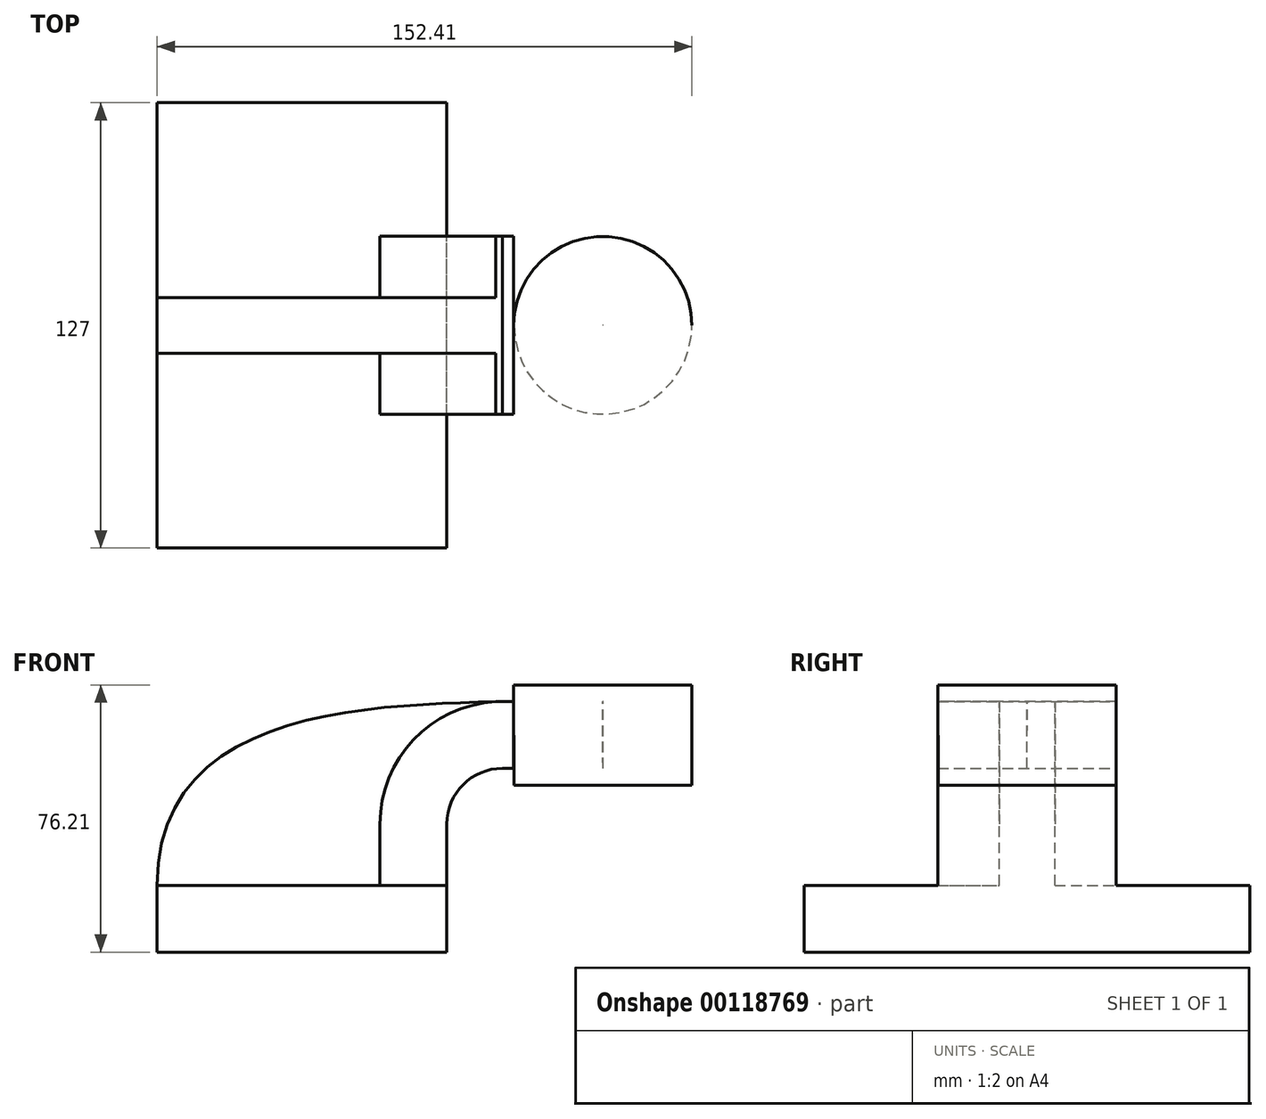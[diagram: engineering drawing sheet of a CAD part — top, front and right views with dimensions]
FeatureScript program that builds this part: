
annotation { "Feature Type Name" : "Feature", "Feature Type Description" : "" }
export const myFeature = defineFeature(function(context is Context, id is Id, definition is map)
    precondition{}
    {
        {
            var Q0;
            Q0=qCreatedBy(makeId("Front.planeOp"),FACE);
            var sketch = newSketch(context, id + "F0", { "sketchPlane" : qUnion([Q0])});
            skLineSegment(sketch, "E0.bottom", {"start": v(-41.28, 9.53) * mm, "end": v(41.28, 9.53) * mm});
            skLineSegment(sketch, "E0.top", {"start": v(-41.28, -9.53) * mm, "end": v(41.28, -9.53) * mm});
            skLineSegment(sketch, "E0.left", {"start": v(-41.28, 9.52) * mm, "end": v(-41.28, -9.53) * mm});
            skLineSegment(sketch, "E0.right", {"start": v(41.27, 9.53) * mm, "end": v(41.27, -9.52) * mm});
            skPoint(sketch, "E0.middle", {"position": v(0, 0) * mm});
            skLineSegment(sketch, "E1.bottom", {"start": v(111.12, 66.67) * mm, "end": v(60.32, 66.67) * mm});
            skLineSegment(sketch, "E1.top", {"start": v(111.12, 38.1) * mm, "end": v(85.79, 38.1) * mm});
            skLineSegment(sketch, "E1.left", {"start": v(111.12, 66.68) * mm, "end": v(111.12, 38.1) * mm});
            skLineSegment(sketch, "E1.right", {"start": v(60.32, 66.68) * mm, "end": v(60.32, 38.1) * mm});
            skPoint(sketch, "E1.middle", {"position": v(85.72, 52.39) * mm});
            skLineSegment(sketch, "E2", {"start": v(41.27, 9.53) * mm, "end": v(41.27, 27) * mm});
            skArc(sketch, "E3", {"start": v(41.27, 27) * mm, "mid": v(45.92, 38.23) * mm, "end": v(57.15, 42.88) * mm});
            skLineSegment(sketch, "E4.0", {"start": v(57.15, 61.93) * mm, "end": v(85.79, 61.93) * mm});
            skArc(sketch, "E4.1", {"start": v(22.22, 27) * mm, "mid": v(32.45, 51.7) * mm, "end": v(57.15, 61.93) * mm});
            skLineSegment(sketch, "E4.2", {"start": v(22.22, 9.53) * mm, "end": v(22.22, 27) * mm});
            skFitSpline(sketch, "E5", {"points": [v(-41.28, 9.52) * mm, v(57.15, 61.93) * mm], "startDerivative": vector(-0.32, 154.05) * mm, "endDerivative": vector(107.42, 3.15) * mm});
            skLineSegment(sketch, "E6", {"start": v(85.73, 66.67) * mm, "end": v(85.79, 38.1) * mm});
            skPoint(sketch, "E7.end.orphan", {"position": v(85.72, 42.88) * mm});
            skLineSegment(sketch, "E8", {"start": v(57.15, 42.88) * mm, "end": v(85.72, 42.88) * mm});
            skLineSegment(sketch, "E9", {"start": v(60.32, 38.1) * mm, "end": v(85.79, 38.1) * mm});
            skLineSegment(sketch, "E10.bottom", {"start": v(60.32, 42.88) * mm, "end": v(85.79, 42.88) * mm});
            skLineSegment(sketch, "E10.top", {"start": v(60.32, 61.93) * mm, "end": v(85.79, 61.93) * mm});
            skLineSegment(sketch, "E10.left", {"start": v(60.32, 42.88) * mm, "end": v(60.32, 61.93) * mm});
            skLineSegment(sketch, "E10.right", {"start": v(85.79, 42.88) * mm, "end": v(85.79, 61.93) * mm});
            skSolve(sketch);
        }
        {
            var Q0;
            Q0=makeQuery(id+"F0.imprint","IMPRINT",FACE,{"disambiguationData":[TD([[makeQuery(id+"F0.imprint","IMPRINT",EDGE,{"derivedFrom":sQuery(id+"F0.wireOp",EDGE,"E0.top")}),1.0]])]});
            extrude(context, id + "F1", {"entities" : qUnion([Q0]), "endBound" : BoundingType.SYMMETRIC, "depth" : 127 * mm});
        }
        {
            var Q0;
            {var subQ2=sQuery(id+"F0.wireOp",EDGE,"E2");Q0=makeQuery(id+"F0.imprint","IMPRINT",FACE,{"disambiguationData":[TD([[makeQuery(id+"F0.imprint","IMPRINT",EDGE,{"derivedFrom":subQ2}),1.0]])]});}
            var Q1;
            {var subQ0=sQuery(id+"F0.wireOp",EDGE,"E10.left");Q1=makeQuery(id+"F0.imprint","IMPRINT",FACE,{"disambiguationData":[TD([[makeQuery(id+"F0.imprint","IMPRINT",EDGE,{"derivedFrom":subQ0}),-1.0]])]});}
            extrude(context, id + "F2", {"entities" : qUnion([Q0, Q1]), "operationType" : NewBodyOperationType.ADD, "endBound" : BoundingType.SYMMETRIC, "depth" : 50.8 * mm});
        }
        {
            var Q0;
            {var subQ3=sQuery(id+"F0.wireOp",EDGE,"E4.2");Q0=makeQuery(id+"F0.imprint","IMPRINT",FACE,{"disambiguationData":[TD([[makeQuery(id+"F0.imprint","IMPRINT",EDGE,{"derivedFrom":subQ3}),1.0]])]});}
            extrude(context, id + "F3", {"entities" : qUnion([Q0]), "operationType" : NewBodyOperationType.ADD, "endBound" : BoundingType.SYMMETRIC, "depth" : 15.88 * mm});
        }
        {
            var Q0;
            {var subQ4=sQuery(id+"F0.wireOp",EDGE,"E1.left");Q0=makeQuery(id+"F0.imprint","IMPRINT",FACE,{"disambiguationData":[TD([[makeQuery(id+"F0.imprint","IMPRINT",EDGE,{"derivedFrom":subQ4}),-1.0]])]});}
            var Q1;
            Q1=sQuery(id+"F0.wireOp",EDGE,"E6");
            revolve(context, id + "F4", {"entities" : qUnion([Q0]), "axis" : qUnion([Q1]), "revolveType" : RevolveType.FULL});
        }
    });
